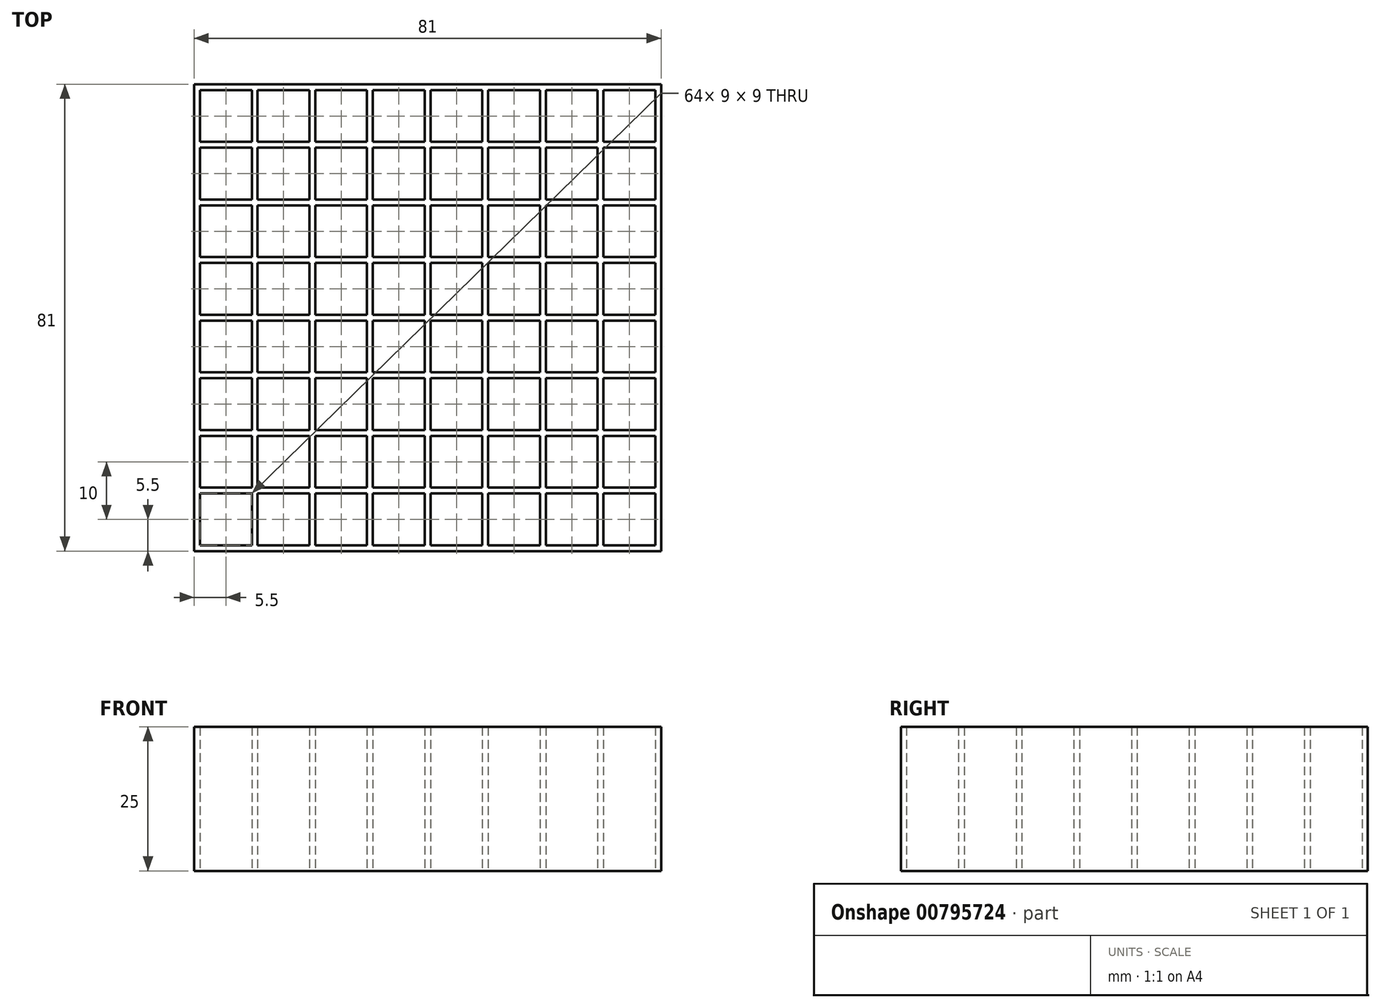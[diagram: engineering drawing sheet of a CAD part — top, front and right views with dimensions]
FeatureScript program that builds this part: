
annotation { "Feature Type Name" : "Feature", "Feature Type Description" : "" }
export const myFeature = defineFeature(function(context is Context, id is Id, definition is map)
    precondition{}
    {
        {
            var Q0;
            Q0=qCreatedBy(makeId("Top.planeOp"),FACE);
            var sketch = newSketch(context, id + "F0", { "sketchPlane" : qUnion([Q0])});
            skLineSegment(sketch, "E0.bottom", {"start": v(-40.5, 40.5) * mm, "end": v(40.5, 40.5) * mm});
            skLineSegment(sketch, "E0.top", {"start": v(-40.5, -40.5) * mm, "end": v(40.5, -40.5) * mm});
            skLineSegment(sketch, "E0.left", {"start": v(-40.5, 40.5) * mm, "end": v(-40.5, -40.5) * mm});
            skLineSegment(sketch, "E0.right", {"start": v(40.5, 40.5) * mm, "end": v(40.5, -40.5) * mm});
            skPoint(sketch, "E1", {"position": v(-40.5, 0) * mm});
            skPoint(sketch, "E2", {"position": v(0, 40.5) * mm});
            skLineSegment(sketch, "E3.bottom", {"start": v(-39.5, 39.5) * mm, "end": v(-30.5, 39.5) * mm});
            skLineSegment(sketch, "E3.top", {"start": v(-39.5, 30.5) * mm, "end": v(-30.5, 30.5) * mm});
            skLineSegment(sketch, "E3.left", {"start": v(-39.5, 39.5) * mm, "end": v(-39.5, 30.5) * mm});
            skLineSegment(sketch, "E3.right", {"start": v(-30.5, 39.5) * mm, "end": v(-30.5, 30.5) * mm});
            skLineSegment(sketch, "E4.1.0.0", {"start": v(-20.5, 39.5) * mm, "end": v(-20.5, 30.5) * mm});
            skLineSegment(sketch, "E4.1.0.1", {"start": v(-29.5, 39.5) * mm, "end": v(-20.5, 39.5) * mm});
            skLineSegment(sketch, "E4.1.0.2", {"start": v(-29.5, 39.5) * mm, "end": v(-29.5, 30.5) * mm});
            skLineSegment(sketch, "E4.1.0.3", {"start": v(-29.5, 30.5) * mm, "end": v(-20.5, 30.5) * mm});
            skLineSegment(sketch, "E4.2.0.0", {"start": v(-10.5, 39.5) * mm, "end": v(-10.5, 30.5) * mm});
            skLineSegment(sketch, "E4.2.0.1", {"start": v(-19.5, 39.5) * mm, "end": v(-10.5, 39.5) * mm});
            skLineSegment(sketch, "E4.2.0.2", {"start": v(-19.5, 39.5) * mm, "end": v(-19.5, 30.5) * mm});
            skLineSegment(sketch, "E4.2.0.3", {"start": v(-19.5, 30.5) * mm, "end": v(-10.5, 30.5) * mm});
            skLineSegment(sketch, "E4.3.0.0", {"start": v(-0.5, 39.5) * mm, "end": v(-0.5, 30.5) * mm});
            skLineSegment(sketch, "E4.3.0.1", {"start": v(-9.5, 39.5) * mm, "end": v(-0.5, 39.5) * mm});
            skLineSegment(sketch, "E4.3.0.2", {"start": v(-9.5, 39.5) * mm, "end": v(-9.5, 30.5) * mm});
            skLineSegment(sketch, "E4.3.0.3", {"start": v(-9.5, 30.5) * mm, "end": v(-0.5, 30.5) * mm});
            skLineSegment(sketch, "E4.4.0.0", {"start": v(9.5, 39.5) * mm, "end": v(9.5, 30.5) * mm});
            skLineSegment(sketch, "E4.4.0.1", {"start": v(0.5, 39.5) * mm, "end": v(9.5, 39.5) * mm});
            skLineSegment(sketch, "E4.4.0.2", {"start": v(0.5, 39.5) * mm, "end": v(0.5, 30.5) * mm});
            skLineSegment(sketch, "E4.4.0.3", {"start": v(0.5, 30.5) * mm, "end": v(9.5, 30.5) * mm});
            skLineSegment(sketch, "E4.5.0.0", {"start": v(19.5, 39.5) * mm, "end": v(19.5, 30.5) * mm});
            skLineSegment(sketch, "E4.5.0.1", {"start": v(10.5, 39.5) * mm, "end": v(19.5, 39.5) * mm});
            skLineSegment(sketch, "E4.5.0.2", {"start": v(10.5, 39.5) * mm, "end": v(10.5, 30.5) * mm});
            skLineSegment(sketch, "E4.5.0.3", {"start": v(10.5, 30.5) * mm, "end": v(19.5, 30.5) * mm});
            skLineSegment(sketch, "E4.6.0.0", {"start": v(29.5, 39.5) * mm, "end": v(29.5, 30.5) * mm});
            skLineSegment(sketch, "E4.6.0.1", {"start": v(20.5, 39.5) * mm, "end": v(29.5, 39.5) * mm});
            skLineSegment(sketch, "E4.6.0.2", {"start": v(20.5, 39.5) * mm, "end": v(20.5, 30.5) * mm});
            skLineSegment(sketch, "E4.6.0.3", {"start": v(20.5, 30.5) * mm, "end": v(29.5, 30.5) * mm});
            skLineSegment(sketch, "E4.7.0.0", {"start": v(39.5, 39.5) * mm, "end": v(39.5, 30.5) * mm});
            skLineSegment(sketch, "E4.7.0.1", {"start": v(30.5, 39.5) * mm, "end": v(39.5, 39.5) * mm});
            skLineSegment(sketch, "E4.7.0.2", {"start": v(30.5, 39.5) * mm, "end": v(30.5, 30.5) * mm});
            skLineSegment(sketch, "E4.7.0.3", {"start": v(30.5, 30.5) * mm, "end": v(39.5, 30.5) * mm});
            skLineSegment(sketch, "E4.direction1", {"start": v(-39.5, 30.5) * mm, "end": v(-29.5, 30.5) * mm, "construction": true});
            skLineSegment(sketch, "E5.0.1.0", {"start": v(-19.5, 20.5) * mm, "end": v(-10.5, 20.5) * mm});
            skLineSegment(sketch, "E5.0.1.1", {"start": v(-19.5, 29.5) * mm, "end": v(-19.5, 20.5) * mm});
            skLineSegment(sketch, "E5.0.1.2", {"start": v(-39.5, 29.5) * mm, "end": v(-30.5, 29.5) * mm});
            skLineSegment(sketch, "E5.0.1.3", {"start": v(-39.5, 29.5) * mm, "end": v(-39.5, 20.5) * mm});
            skLineSegment(sketch, "E5.0.1.4", {"start": v(10.5, 29.5) * mm, "end": v(10.5, 20.5) * mm});
            skLineSegment(sketch, "E5.0.1.5", {"start": v(-30.5, 29.5) * mm, "end": v(-30.5, 20.5) * mm});
            skLineSegment(sketch, "E5.0.1.6", {"start": v(-9.5, 20.5) * mm, "end": v(-0.5, 20.5) * mm});
            skLineSegment(sketch, "E5.0.1.7", {"start": v(-20.5, 29.5) * mm, "end": v(-20.5, 20.5) * mm});
            skLineSegment(sketch, "E5.0.1.8", {"start": v(-29.5, 29.5) * mm, "end": v(-20.5, 29.5) * mm});
            skLineSegment(sketch, "E5.0.1.9", {"start": v(-29.5, 29.5) * mm, "end": v(-29.5, 20.5) * mm});
            skLineSegment(sketch, "E5.0.1.10", {"start": v(-29.5, 20.5) * mm, "end": v(-20.5, 20.5) * mm});
            skLineSegment(sketch, "E5.0.1.11", {"start": v(-10.5, 29.5) * mm, "end": v(-10.5, 20.5) * mm});
            skLineSegment(sketch, "E5.0.1.12", {"start": v(10.5, 20.5) * mm, "end": v(19.5, 20.5) * mm});
            skLineSegment(sketch, "E5.0.1.13", {"start": v(0.5, 20.5) * mm, "end": v(9.5, 20.5) * mm});
            skLineSegment(sketch, "E5.0.1.14", {"start": v(9.5, 29.5) * mm, "end": v(9.5, 20.5) * mm});
            skPoint(sketch, "E5.0.1.15", {"position": v(0, 30.5) * mm});
            skLineSegment(sketch, "E5.0.1.16", {"start": v(20.5, 29.5) * mm, "end": v(29.5, 29.5) * mm});
            skLineSegment(sketch, "E5.0.1.17", {"start": v(-39.5, 20.5) * mm, "end": v(-29.5, 20.5) * mm, "construction": true});
            skLineSegment(sketch, "E5.0.1.18", {"start": v(30.5, 20.5) * mm, "end": v(39.5, 20.5) * mm});
            skLineSegment(sketch, "E5.0.1.19", {"start": v(-0.5, 29.5) * mm, "end": v(-0.5, 20.5) * mm});
            skLineSegment(sketch, "E5.0.1.20", {"start": v(39.5, 29.5) * mm, "end": v(39.5, 20.5) * mm});
            skLineSegment(sketch, "E5.0.1.21", {"start": v(29.5, 29.5) * mm, "end": v(29.5, 20.5) * mm});
            skLineSegment(sketch, "E5.0.1.22", {"start": v(19.5, 29.5) * mm, "end": v(19.5, 20.5) * mm});
            skLineSegment(sketch, "E5.0.1.23", {"start": v(0.5, 29.5) * mm, "end": v(9.5, 29.5) * mm});
            skLineSegment(sketch, "E5.0.1.24", {"start": v(20.5, 29.5) * mm, "end": v(20.5, 20.5) * mm});
            skLineSegment(sketch, "E5.0.1.25", {"start": v(-9.5, 29.5) * mm, "end": v(-0.5, 29.5) * mm});
            skLineSegment(sketch, "E5.0.1.26", {"start": v(30.5, 29.5) * mm, "end": v(39.5, 29.5) * mm});
            skLineSegment(sketch, "E5.0.1.27", {"start": v(-19.5, 29.5) * mm, "end": v(-10.5, 29.5) * mm});
            skLineSegment(sketch, "E5.0.1.28", {"start": v(10.5, 29.5) * mm, "end": v(19.5, 29.5) * mm});
            skLineSegment(sketch, "E5.0.1.29", {"start": v(0.5, 29.5) * mm, "end": v(0.5, 20.5) * mm});
            skLineSegment(sketch, "E5.0.1.30", {"start": v(20.5, 20.5) * mm, "end": v(29.5, 20.5) * mm});
            skLineSegment(sketch, "E5.0.1.31", {"start": v(-9.5, 29.5) * mm, "end": v(-9.5, 20.5) * mm});
            skLineSegment(sketch, "E5.0.1.32", {"start": v(30.5, 29.5) * mm, "end": v(30.5, 20.5) * mm});
            skLineSegment(sketch, "E5.0.1.33", {"start": v(-39.5, 20.5) * mm, "end": v(-30.5, 20.5) * mm});
            skLineSegment(sketch, "E5.0.2.0", {"start": v(-19.5, 10.5) * mm, "end": v(-10.5, 10.5) * mm});
            skLineSegment(sketch, "E5.0.2.1", {"start": v(-19.5, 19.5) * mm, "end": v(-19.5, 10.5) * mm});
            skLineSegment(sketch, "E5.0.2.2", {"start": v(-39.5, 19.5) * mm, "end": v(-30.5, 19.5) * mm});
            skLineSegment(sketch, "E5.0.2.3", {"start": v(-39.5, 19.5) * mm, "end": v(-39.5, 10.5) * mm});
            skLineSegment(sketch, "E5.0.2.4", {"start": v(10.5, 19.5) * mm, "end": v(10.5, 10.5) * mm});
            skLineSegment(sketch, "E5.0.2.5", {"start": v(-30.5, 19.5) * mm, "end": v(-30.5, 10.5) * mm});
            skLineSegment(sketch, "E5.0.2.6", {"start": v(-9.5, 10.5) * mm, "end": v(-0.5, 10.5) * mm});
            skLineSegment(sketch, "E5.0.2.7", {"start": v(-20.5, 19.5) * mm, "end": v(-20.5, 10.5) * mm});
            skLineSegment(sketch, "E5.0.2.8", {"start": v(-29.5, 19.5) * mm, "end": v(-20.5, 19.5) * mm});
            skLineSegment(sketch, "E5.0.2.9", {"start": v(-29.5, 19.5) * mm, "end": v(-29.5, 10.5) * mm});
            skLineSegment(sketch, "E5.0.2.10", {"start": v(-29.5, 10.5) * mm, "end": v(-20.5, 10.5) * mm});
            skLineSegment(sketch, "E5.0.2.11", {"start": v(-10.5, 19.5) * mm, "end": v(-10.5, 10.5) * mm});
            skLineSegment(sketch, "E5.0.2.12", {"start": v(10.5, 10.5) * mm, "end": v(19.5, 10.5) * mm});
            skLineSegment(sketch, "E5.0.2.13", {"start": v(0.5, 10.5) * mm, "end": v(9.5, 10.5) * mm});
            skLineSegment(sketch, "E5.0.2.14", {"start": v(9.5, 19.5) * mm, "end": v(9.5, 10.5) * mm});
            skPoint(sketch, "E5.0.2.15", {"position": v(0, 20.5) * mm});
            skLineSegment(sketch, "E5.0.2.16", {"start": v(20.5, 19.5) * mm, "end": v(29.5, 19.5) * mm});
            skLineSegment(sketch, "E5.0.2.17", {"start": v(-39.5, 10.5) * mm, "end": v(-29.5, 10.5) * mm, "construction": true});
            skLineSegment(sketch, "E5.0.2.18", {"start": v(30.5, 10.5) * mm, "end": v(39.5, 10.5) * mm});
            skLineSegment(sketch, "E5.0.2.19", {"start": v(-0.5, 19.5) * mm, "end": v(-0.5, 10.5) * mm});
            skLineSegment(sketch, "E5.0.2.20", {"start": v(39.5, 19.5) * mm, "end": v(39.5, 10.5) * mm});
            skLineSegment(sketch, "E5.0.2.21", {"start": v(29.5, 19.5) * mm, "end": v(29.5, 10.5) * mm});
            skLineSegment(sketch, "E5.0.2.22", {"start": v(19.5, 19.5) * mm, "end": v(19.5, 10.5) * mm});
            skLineSegment(sketch, "E5.0.2.23", {"start": v(0.5, 19.5) * mm, "end": v(9.5, 19.5) * mm});
            skLineSegment(sketch, "E5.0.2.24", {"start": v(20.5, 19.5) * mm, "end": v(20.5, 10.5) * mm});
            skLineSegment(sketch, "E5.0.2.25", {"start": v(-9.5, 19.5) * mm, "end": v(-0.5, 19.5) * mm});
            skLineSegment(sketch, "E5.0.2.26", {"start": v(30.5, 19.5) * mm, "end": v(39.5, 19.5) * mm});
            skLineSegment(sketch, "E5.0.2.27", {"start": v(-19.5, 19.5) * mm, "end": v(-10.5, 19.5) * mm});
            skLineSegment(sketch, "E5.0.2.28", {"start": v(10.5, 19.5) * mm, "end": v(19.5, 19.5) * mm});
            skLineSegment(sketch, "E5.0.2.29", {"start": v(0.5, 19.5) * mm, "end": v(0.5, 10.5) * mm});
            skLineSegment(sketch, "E5.0.2.30", {"start": v(20.5, 10.5) * mm, "end": v(29.5, 10.5) * mm});
            skLineSegment(sketch, "E5.0.2.31", {"start": v(-9.5, 19.5) * mm, "end": v(-9.5, 10.5) * mm});
            skLineSegment(sketch, "E5.0.2.32", {"start": v(30.5, 19.5) * mm, "end": v(30.5, 10.5) * mm});
            skLineSegment(sketch, "E5.0.2.33", {"start": v(-39.5, 10.5) * mm, "end": v(-30.5, 10.5) * mm});
            skLineSegment(sketch, "E5.0.3.0", {"start": v(-19.5, 0.5) * mm, "end": v(-10.5, 0.5) * mm});
            skLineSegment(sketch, "E5.0.3.1", {"start": v(-19.5, 9.5) * mm, "end": v(-19.5, 0.5) * mm});
            skLineSegment(sketch, "E5.0.3.2", {"start": v(-39.5, 9.5) * mm, "end": v(-30.5, 9.5) * mm});
            skLineSegment(sketch, "E5.0.3.3", {"start": v(-39.5, 9.5) * mm, "end": v(-39.5, 0.5) * mm});
            skLineSegment(sketch, "E5.0.3.4", {"start": v(10.5, 9.5) * mm, "end": v(10.5, 0.5) * mm});
            skLineSegment(sketch, "E5.0.3.5", {"start": v(-30.5, 9.5) * mm, "end": v(-30.5, 0.5) * mm});
            skLineSegment(sketch, "E5.0.3.6", {"start": v(-9.5, 0.5) * mm, "end": v(-0.5, 0.5) * mm});
            skLineSegment(sketch, "E5.0.3.7", {"start": v(-20.5, 9.5) * mm, "end": v(-20.5, 0.5) * mm});
            skLineSegment(sketch, "E5.0.3.8", {"start": v(-29.5, 9.5) * mm, "end": v(-20.5, 9.5) * mm});
            skLineSegment(sketch, "E5.0.3.9", {"start": v(-29.5, 9.5) * mm, "end": v(-29.5, 0.5) * mm});
            skLineSegment(sketch, "E5.0.3.10", {"start": v(-29.5, 0.5) * mm, "end": v(-20.5, 0.5) * mm});
            skLineSegment(sketch, "E5.0.3.11", {"start": v(-10.5, 9.5) * mm, "end": v(-10.5, 0.5) * mm});
            skLineSegment(sketch, "E5.0.3.12", {"start": v(10.5, 0.5) * mm, "end": v(19.5, 0.5) * mm});
            skLineSegment(sketch, "E5.0.3.13", {"start": v(0.5, 0.5) * mm, "end": v(9.5, 0.5) * mm});
            skLineSegment(sketch, "E5.0.3.14", {"start": v(9.5, 9.5) * mm, "end": v(9.5, 0.5) * mm});
            skPoint(sketch, "E5.0.3.15", {"position": v(0, 10.5) * mm});
            skLineSegment(sketch, "E5.0.3.16", {"start": v(20.5, 9.5) * mm, "end": v(29.5, 9.5) * mm});
            skLineSegment(sketch, "E5.0.3.17", {"start": v(-39.5, 0.5) * mm, "end": v(-29.5, 0.5) * mm, "construction": true});
            skLineSegment(sketch, "E5.0.3.18", {"start": v(30.5, 0.5) * mm, "end": v(39.5, 0.5) * mm});
            skLineSegment(sketch, "E5.0.3.19", {"start": v(-0.5, 9.5) * mm, "end": v(-0.5, 0.5) * mm});
            skLineSegment(sketch, "E5.0.3.20", {"start": v(39.5, 9.5) * mm, "end": v(39.5, 0.5) * mm});
            skLineSegment(sketch, "E5.0.3.21", {"start": v(29.5, 9.5) * mm, "end": v(29.5, 0.5) * mm});
            skLineSegment(sketch, "E5.0.3.22", {"start": v(19.5, 9.5) * mm, "end": v(19.5, 0.5) * mm});
            skLineSegment(sketch, "E5.0.3.23", {"start": v(0.5, 9.5) * mm, "end": v(9.5, 9.5) * mm});
            skLineSegment(sketch, "E5.0.3.24", {"start": v(20.5, 9.5) * mm, "end": v(20.5, 0.5) * mm});
            skLineSegment(sketch, "E5.0.3.25", {"start": v(-9.5, 9.5) * mm, "end": v(-0.5, 9.5) * mm});
            skLineSegment(sketch, "E5.0.3.26", {"start": v(30.5, 9.5) * mm, "end": v(39.5, 9.5) * mm});
            skLineSegment(sketch, "E5.0.3.27", {"start": v(-19.5, 9.5) * mm, "end": v(-10.5, 9.5) * mm});
            skLineSegment(sketch, "E5.0.3.28", {"start": v(10.5, 9.5) * mm, "end": v(19.5, 9.5) * mm});
            skLineSegment(sketch, "E5.0.3.29", {"start": v(0.5, 9.5) * mm, "end": v(0.5, 0.5) * mm});
            skLineSegment(sketch, "E5.0.3.30", {"start": v(20.5, 0.5) * mm, "end": v(29.5, 0.5) * mm});
            skLineSegment(sketch, "E5.0.3.31", {"start": v(-9.5, 9.5) * mm, "end": v(-9.5, 0.5) * mm});
            skLineSegment(sketch, "E5.0.3.32", {"start": v(30.5, 9.5) * mm, "end": v(30.5, 0.5) * mm});
            skLineSegment(sketch, "E5.0.3.33", {"start": v(-39.5, 0.5) * mm, "end": v(-30.5, 0.5) * mm});
            skLineSegment(sketch, "E5.0.4.0", {"start": v(-19.5, -9.5) * mm, "end": v(-10.5, -9.5) * mm});
            skLineSegment(sketch, "E5.0.4.1", {"start": v(-19.5, -0.5) * mm, "end": v(-19.5, -9.5) * mm});
            skLineSegment(sketch, "E5.0.4.2", {"start": v(-39.5, -0.5) * mm, "end": v(-30.5, -0.5) * mm});
            skLineSegment(sketch, "E5.0.4.3", {"start": v(-39.5, -0.5) * mm, "end": v(-39.5, -9.5) * mm});
            skLineSegment(sketch, "E5.0.4.4", {"start": v(10.5, -0.5) * mm, "end": v(10.5, -9.5) * mm});
            skLineSegment(sketch, "E5.0.4.5", {"start": v(-30.5, -0.5) * mm, "end": v(-30.5, -9.5) * mm});
            skLineSegment(sketch, "E5.0.4.6", {"start": v(-9.5, -9.5) * mm, "end": v(-0.5, -9.5) * mm});
            skLineSegment(sketch, "E5.0.4.7", {"start": v(-20.5, -0.5) * mm, "end": v(-20.5, -9.5) * mm});
            skLineSegment(sketch, "E5.0.4.8", {"start": v(-29.5, -0.5) * mm, "end": v(-20.5, -0.5) * mm});
            skLineSegment(sketch, "E5.0.4.9", {"start": v(-29.5, -0.5) * mm, "end": v(-29.5, -9.5) * mm});
            skLineSegment(sketch, "E5.0.4.10", {"start": v(-29.5, -9.5) * mm, "end": v(-20.5, -9.5) * mm});
            skLineSegment(sketch, "E5.0.4.11", {"start": v(-10.5, -0.5) * mm, "end": v(-10.5, -9.5) * mm});
            skLineSegment(sketch, "E5.0.4.12", {"start": v(10.5, -9.5) * mm, "end": v(19.5, -9.5) * mm});
            skLineSegment(sketch, "E5.0.4.13", {"start": v(0.5, -9.5) * mm, "end": v(9.5, -9.5) * mm});
            skLineSegment(sketch, "E5.0.4.14", {"start": v(9.5, -0.5) * mm, "end": v(9.5, -9.5) * mm});
            skPoint(sketch, "E5.0.4.15", {"position": v(0, 0.5) * mm});
            skLineSegment(sketch, "E5.0.4.16", {"start": v(20.5, -0.5) * mm, "end": v(29.5, -0.5) * mm});
            skLineSegment(sketch, "E5.0.4.17", {"start": v(-39.5, -9.5) * mm, "end": v(-29.5, -9.5) * mm, "construction": true});
            skLineSegment(sketch, "E5.0.4.18", {"start": v(30.5, -9.5) * mm, "end": v(39.5, -9.5) * mm});
            skLineSegment(sketch, "E5.0.4.19", {"start": v(-0.5, -0.5) * mm, "end": v(-0.5, -9.5) * mm});
            skLineSegment(sketch, "E5.0.4.20", {"start": v(39.5, -0.5) * mm, "end": v(39.5, -9.5) * mm});
            skLineSegment(sketch, "E5.0.4.21", {"start": v(29.5, -0.5) * mm, "end": v(29.5, -9.5) * mm});
            skLineSegment(sketch, "E5.0.4.22", {"start": v(19.5, -0.5) * mm, "end": v(19.5, -9.5) * mm});
            skLineSegment(sketch, "E5.0.4.23", {"start": v(0.5, -0.5) * mm, "end": v(9.5, -0.5) * mm});
            skLineSegment(sketch, "E5.0.4.24", {"start": v(20.5, -0.5) * mm, "end": v(20.5, -9.5) * mm});
            skLineSegment(sketch, "E5.0.4.25", {"start": v(-9.5, -0.5) * mm, "end": v(-0.5, -0.5) * mm});
            skLineSegment(sketch, "E5.0.4.26", {"start": v(30.5, -0.5) * mm, "end": v(39.5, -0.5) * mm});
            skLineSegment(sketch, "E5.0.4.27", {"start": v(-19.5, -0.5) * mm, "end": v(-10.5, -0.5) * mm});
            skLineSegment(sketch, "E5.0.4.28", {"start": v(10.5, -0.5) * mm, "end": v(19.5, -0.5) * mm});
            skLineSegment(sketch, "E5.0.4.29", {"start": v(0.5, -0.5) * mm, "end": v(0.5, -9.5) * mm});
            skLineSegment(sketch, "E5.0.4.30", {"start": v(20.5, -9.5) * mm, "end": v(29.5, -9.5) * mm});
            skLineSegment(sketch, "E5.0.4.31", {"start": v(-9.5, -0.5) * mm, "end": v(-9.5, -9.5) * mm});
            skLineSegment(sketch, "E5.0.4.32", {"start": v(30.5, -0.5) * mm, "end": v(30.5, -9.5) * mm});
            skLineSegment(sketch, "E5.0.4.33", {"start": v(-39.5, -9.5) * mm, "end": v(-30.5, -9.5) * mm});
            skLineSegment(sketch, "E5.0.5.0", {"start": v(-19.5, -19.5) * mm, "end": v(-10.5, -19.5) * mm});
            skLineSegment(sketch, "E5.0.5.1", {"start": v(-19.5, -10.5) * mm, "end": v(-19.5, -19.5) * mm});
            skLineSegment(sketch, "E5.0.5.2", {"start": v(-39.5, -10.5) * mm, "end": v(-30.5, -10.5) * mm});
            skLineSegment(sketch, "E5.0.5.3", {"start": v(-39.5, -10.5) * mm, "end": v(-39.5, -19.5) * mm});
            skLineSegment(sketch, "E5.0.5.4", {"start": v(10.5, -10.5) * mm, "end": v(10.5, -19.5) * mm});
            skLineSegment(sketch, "E5.0.5.5", {"start": v(-30.5, -10.5) * mm, "end": v(-30.5, -19.5) * mm});
            skLineSegment(sketch, "E5.0.5.6", {"start": v(-9.5, -19.5) * mm, "end": v(-0.5, -19.5) * mm});
            skLineSegment(sketch, "E5.0.5.7", {"start": v(-20.5, -10.5) * mm, "end": v(-20.5, -19.5) * mm});
            skLineSegment(sketch, "E5.0.5.8", {"start": v(-29.5, -10.5) * mm, "end": v(-20.5, -10.5) * mm});
            skLineSegment(sketch, "E5.0.5.9", {"start": v(-29.5, -10.5) * mm, "end": v(-29.5, -19.5) * mm});
            skLineSegment(sketch, "E5.0.5.10", {"start": v(-29.5, -19.5) * mm, "end": v(-20.5, -19.5) * mm});
            skLineSegment(sketch, "E5.0.5.11", {"start": v(-10.5, -10.5) * mm, "end": v(-10.5, -19.5) * mm});
            skLineSegment(sketch, "E5.0.5.12", {"start": v(10.5, -19.5) * mm, "end": v(19.5, -19.5) * mm});
            skLineSegment(sketch, "E5.0.5.13", {"start": v(0.5, -19.5) * mm, "end": v(9.5, -19.5) * mm});
            skLineSegment(sketch, "E5.0.5.14", {"start": v(9.5, -10.5) * mm, "end": v(9.5, -19.5) * mm});
            skPoint(sketch, "E5.0.5.15", {"position": v(0, -9.5) * mm});
            skLineSegment(sketch, "E5.0.5.16", {"start": v(20.5, -10.5) * mm, "end": v(29.5, -10.5) * mm});
            skLineSegment(sketch, "E5.0.5.17", {"start": v(-39.5, -19.5) * mm, "end": v(-29.5, -19.5) * mm, "construction": true});
            skLineSegment(sketch, "E5.0.5.18", {"start": v(30.5, -19.5) * mm, "end": v(39.5, -19.5) * mm});
            skLineSegment(sketch, "E5.0.5.19", {"start": v(-0.5, -10.5) * mm, "end": v(-0.5, -19.5) * mm});
            skLineSegment(sketch, "E5.0.5.20", {"start": v(39.5, -10.5) * mm, "end": v(39.5, -19.5) * mm});
            skLineSegment(sketch, "E5.0.5.21", {"start": v(29.5, -10.5) * mm, "end": v(29.5, -19.5) * mm});
            skLineSegment(sketch, "E5.0.5.22", {"start": v(19.5, -10.5) * mm, "end": v(19.5, -19.5) * mm});
            skLineSegment(sketch, "E5.0.5.23", {"start": v(0.5, -10.5) * mm, "end": v(9.5, -10.5) * mm});
            skLineSegment(sketch, "E5.0.5.24", {"start": v(20.5, -10.5) * mm, "end": v(20.5, -19.5) * mm});
            skLineSegment(sketch, "E5.0.5.25", {"start": v(-9.5, -10.5) * mm, "end": v(-0.5, -10.5) * mm});
            skLineSegment(sketch, "E5.0.5.26", {"start": v(30.5, -10.5) * mm, "end": v(39.5, -10.5) * mm});
            skLineSegment(sketch, "E5.0.5.27", {"start": v(-19.5, -10.5) * mm, "end": v(-10.5, -10.5) * mm});
            skLineSegment(sketch, "E5.0.5.28", {"start": v(10.5, -10.5) * mm, "end": v(19.5, -10.5) * mm});
            skLineSegment(sketch, "E5.0.5.29", {"start": v(0.5, -10.5) * mm, "end": v(0.5, -19.5) * mm});
            skLineSegment(sketch, "E5.0.5.30", {"start": v(20.5, -19.5) * mm, "end": v(29.5, -19.5) * mm});
            skLineSegment(sketch, "E5.0.5.31", {"start": v(-9.5, -10.5) * mm, "end": v(-9.5, -19.5) * mm});
            skLineSegment(sketch, "E5.0.5.32", {"start": v(30.5, -10.5) * mm, "end": v(30.5, -19.5) * mm});
            skLineSegment(sketch, "E5.0.5.33", {"start": v(-39.5, -19.5) * mm, "end": v(-30.5, -19.5) * mm});
            skLineSegment(sketch, "E5.0.6.0", {"start": v(-19.5, -29.5) * mm, "end": v(-10.5, -29.5) * mm});
            skLineSegment(sketch, "E5.0.6.1", {"start": v(-19.5, -20.5) * mm, "end": v(-19.5, -29.5) * mm});
            skLineSegment(sketch, "E5.0.6.2", {"start": v(-39.5, -20.5) * mm, "end": v(-30.5, -20.5) * mm});
            skLineSegment(sketch, "E5.0.6.3", {"start": v(-39.5, -20.5) * mm, "end": v(-39.5, -29.5) * mm});
            skLineSegment(sketch, "E5.0.6.4", {"start": v(10.5, -20.5) * mm, "end": v(10.5, -29.5) * mm});
            skLineSegment(sketch, "E5.0.6.5", {"start": v(-30.5, -20.5) * mm, "end": v(-30.5, -29.5) * mm});
            skLineSegment(sketch, "E5.0.6.6", {"start": v(-9.5, -29.5) * mm, "end": v(-0.5, -29.5) * mm});
            skLineSegment(sketch, "E5.0.6.7", {"start": v(-20.5, -20.5) * mm, "end": v(-20.5, -29.5) * mm});
            skLineSegment(sketch, "E5.0.6.8", {"start": v(-29.5, -20.5) * mm, "end": v(-20.5, -20.5) * mm});
            skLineSegment(sketch, "E5.0.6.9", {"start": v(-29.5, -20.5) * mm, "end": v(-29.5, -29.5) * mm});
            skLineSegment(sketch, "E5.0.6.10", {"start": v(-29.5, -29.5) * mm, "end": v(-20.5, -29.5) * mm});
            skLineSegment(sketch, "E5.0.6.11", {"start": v(-10.5, -20.5) * mm, "end": v(-10.5, -29.5) * mm});
            skLineSegment(sketch, "E5.0.6.12", {"start": v(10.5, -29.5) * mm, "end": v(19.5, -29.5) * mm});
            skLineSegment(sketch, "E5.0.6.13", {"start": v(0.5, -29.5) * mm, "end": v(9.5, -29.5) * mm});
            skLineSegment(sketch, "E5.0.6.14", {"start": v(9.5, -20.5) * mm, "end": v(9.5, -29.5) * mm});
            skPoint(sketch, "E5.0.6.15", {"position": v(0, -19.5) * mm});
            skLineSegment(sketch, "E5.0.6.16", {"start": v(20.5, -20.5) * mm, "end": v(29.5, -20.5) * mm});
            skLineSegment(sketch, "E5.0.6.17", {"start": v(-39.5, -29.5) * mm, "end": v(-29.5, -29.5) * mm, "construction": true});
            skLineSegment(sketch, "E5.0.6.18", {"start": v(30.5, -29.5) * mm, "end": v(39.5, -29.5) * mm});
            skLineSegment(sketch, "E5.0.6.19", {"start": v(-0.5, -20.5) * mm, "end": v(-0.5, -29.5) * mm});
            skLineSegment(sketch, "E5.0.6.20", {"start": v(39.5, -20.5) * mm, "end": v(39.5, -29.5) * mm});
            skLineSegment(sketch, "E5.0.6.21", {"start": v(29.5, -20.5) * mm, "end": v(29.5, -29.5) * mm});
            skLineSegment(sketch, "E5.0.6.22", {"start": v(19.5, -20.5) * mm, "end": v(19.5, -29.5) * mm});
            skLineSegment(sketch, "E5.0.6.23", {"start": v(0.5, -20.5) * mm, "end": v(9.5, -20.5) * mm});
            skLineSegment(sketch, "E5.0.6.24", {"start": v(20.5, -20.5) * mm, "end": v(20.5, -29.5) * mm});
            skLineSegment(sketch, "E5.0.6.25", {"start": v(-9.5, -20.5) * mm, "end": v(-0.5, -20.5) * mm});
            skLineSegment(sketch, "E5.0.6.26", {"start": v(30.5, -20.5) * mm, "end": v(39.5, -20.5) * mm});
            skLineSegment(sketch, "E5.0.6.27", {"start": v(-19.5, -20.5) * mm, "end": v(-10.5, -20.5) * mm});
            skLineSegment(sketch, "E5.0.6.28", {"start": v(10.5, -20.5) * mm, "end": v(19.5, -20.5) * mm});
            skLineSegment(sketch, "E5.0.6.29", {"start": v(0.5, -20.5) * mm, "end": v(0.5, -29.5) * mm});
            skLineSegment(sketch, "E5.0.6.30", {"start": v(20.5, -29.5) * mm, "end": v(29.5, -29.5) * mm});
            skLineSegment(sketch, "E5.0.6.31", {"start": v(-9.5, -20.5) * mm, "end": v(-9.5, -29.5) * mm});
            skLineSegment(sketch, "E5.0.6.32", {"start": v(30.5, -20.5) * mm, "end": v(30.5, -29.5) * mm});
            skLineSegment(sketch, "E5.0.6.33", {"start": v(-39.5, -29.5) * mm, "end": v(-30.5, -29.5) * mm});
            skLineSegment(sketch, "E5.0.7.0", {"start": v(-19.5, -39.5) * mm, "end": v(-10.5, -39.5) * mm});
            skLineSegment(sketch, "E5.0.7.1", {"start": v(-19.5, -30.5) * mm, "end": v(-19.5, -39.5) * mm});
            skLineSegment(sketch, "E5.0.7.2", {"start": v(-39.5, -30.5) * mm, "end": v(-30.5, -30.5) * mm});
            skLineSegment(sketch, "E5.0.7.3", {"start": v(-39.5, -30.5) * mm, "end": v(-39.5, -39.5) * mm});
            skLineSegment(sketch, "E5.0.7.4", {"start": v(10.5, -30.5) * mm, "end": v(10.5, -39.5) * mm});
            skLineSegment(sketch, "E5.0.7.5", {"start": v(-30.5, -30.5) * mm, "end": v(-30.5, -39.5) * mm});
            skLineSegment(sketch, "E5.0.7.6", {"start": v(-9.5, -39.5) * mm, "end": v(-0.5, -39.5) * mm});
            skLineSegment(sketch, "E5.0.7.7", {"start": v(-20.5, -30.5) * mm, "end": v(-20.5, -39.5) * mm});
            skLineSegment(sketch, "E5.0.7.8", {"start": v(-29.5, -30.5) * mm, "end": v(-20.5, -30.5) * mm});
            skLineSegment(sketch, "E5.0.7.9", {"start": v(-29.5, -30.5) * mm, "end": v(-29.5, -39.5) * mm});
            skLineSegment(sketch, "E5.0.7.10", {"start": v(-29.5, -39.5) * mm, "end": v(-20.5, -39.5) * mm});
            skLineSegment(sketch, "E5.0.7.11", {"start": v(-10.5, -30.5) * mm, "end": v(-10.5, -39.5) * mm});
            skLineSegment(sketch, "E5.0.7.12", {"start": v(10.5, -39.5) * mm, "end": v(19.5, -39.5) * mm});
            skLineSegment(sketch, "E5.0.7.13", {"start": v(0.5, -39.5) * mm, "end": v(9.5, -39.5) * mm});
            skLineSegment(sketch, "E5.0.7.14", {"start": v(9.5, -30.5) * mm, "end": v(9.5, -39.5) * mm});
            skPoint(sketch, "E5.0.7.15", {"position": v(0, -29.5) * mm});
            skLineSegment(sketch, "E5.0.7.16", {"start": v(20.5, -30.5) * mm, "end": v(29.5, -30.5) * mm});
            skLineSegment(sketch, "E5.0.7.17", {"start": v(-39.5, -39.5) * mm, "end": v(-29.5, -39.5) * mm, "construction": true});
            skLineSegment(sketch, "E5.0.7.18", {"start": v(30.5, -39.5) * mm, "end": v(39.5, -39.5) * mm});
            skLineSegment(sketch, "E5.0.7.19", {"start": v(-0.5, -30.5) * mm, "end": v(-0.5, -39.5) * mm});
            skLineSegment(sketch, "E5.0.7.20", {"start": v(39.5, -30.5) * mm, "end": v(39.5, -39.5) * mm});
            skLineSegment(sketch, "E5.0.7.21", {"start": v(29.5, -30.5) * mm, "end": v(29.5, -39.5) * mm});
            skLineSegment(sketch, "E5.0.7.22", {"start": v(19.5, -30.5) * mm, "end": v(19.5, -39.5) * mm});
            skLineSegment(sketch, "E5.0.7.23", {"start": v(0.5, -30.5) * mm, "end": v(9.5, -30.5) * mm});
            skLineSegment(sketch, "E5.0.7.24", {"start": v(20.5, -30.5) * mm, "end": v(20.5, -39.5) * mm});
            skLineSegment(sketch, "E5.0.7.25", {"start": v(-9.5, -30.5) * mm, "end": v(-0.5, -30.5) * mm});
            skLineSegment(sketch, "E5.0.7.26", {"start": v(30.5, -30.5) * mm, "end": v(39.5, -30.5) * mm});
            skLineSegment(sketch, "E5.0.7.27", {"start": v(-19.5, -30.5) * mm, "end": v(-10.5, -30.5) * mm});
            skLineSegment(sketch, "E5.0.7.28", {"start": v(10.5, -30.5) * mm, "end": v(19.5, -30.5) * mm});
            skLineSegment(sketch, "E5.0.7.29", {"start": v(0.5, -30.5) * mm, "end": v(0.5, -39.5) * mm});
            skLineSegment(sketch, "E5.0.7.30", {"start": v(20.5, -39.5) * mm, "end": v(29.5, -39.5) * mm});
            skLineSegment(sketch, "E5.0.7.31", {"start": v(-9.5, -30.5) * mm, "end": v(-9.5, -39.5) * mm});
            skLineSegment(sketch, "E5.0.7.32", {"start": v(30.5, -30.5) * mm, "end": v(30.5, -39.5) * mm});
            skLineSegment(sketch, "E5.0.7.33", {"start": v(-39.5, -39.5) * mm, "end": v(-30.5, -39.5) * mm});
            skLineSegment(sketch, "E5.direction1", {"start": v(-39.5, 30.5) * mm, "end": v(-17.6, 30.5) * mm, "construction": true});
            skLineSegment(sketch, "E5.direction2", {"start": v(-39.5, 30.5) * mm, "end": v(-39.5, 20.5) * mm, "construction": true});
            skSolve(sketch);
        }
        {
            var Q0;
            Q0=makeQuery(id+"F0.imprint","IMPRINT",FACE,{"disambiguationData":[TD([[makeQuery(id+"F0.imprint","IMPRINT",EDGE,{"derivedFrom":sQuery(id+"F0.wireOp",EDGE,"E0.bottom")}),-1.0]])]});
            extrude(context, id + "F1", {"entities" : qUnion([Q0]), "depth" : 25 * mm, "offsetDistance" : 25 * mm});
        }
    });
